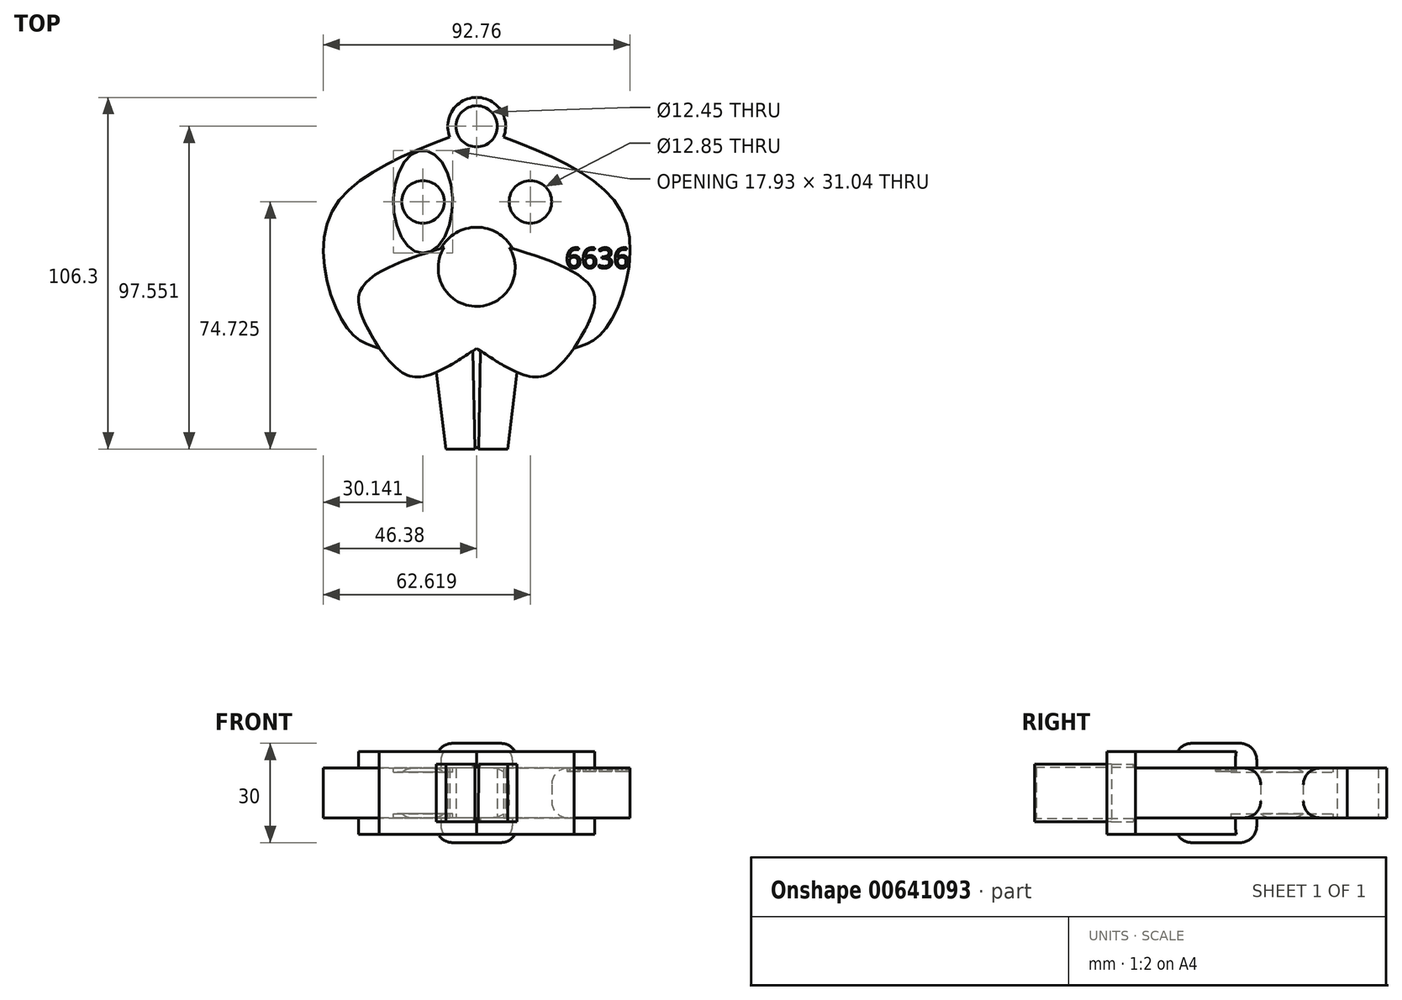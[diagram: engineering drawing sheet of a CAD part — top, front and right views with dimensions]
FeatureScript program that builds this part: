
annotation { "Feature Type Name" : "Feature", "Feature Type Description" : "" }
export const myFeature = defineFeature(function(context is Context, id is Id, definition is map)
    precondition{}
    {
        {
            var Q0;
            Q0=qCreatedBy(makeId("Top.planeOp"),FACE);
            var sketch = newSketch(context, id + "F0", { "sketchPlane" : qUnion([Q0])});
            skCircle(sketch, "E0", {"center": v(0, 42.8) * mm, "radius": 8.75 * mm});
            skFitSpline(sketch, "E1", {"points": [v(-8.15, 39.62) * mm, v(-44.98, 14.23) * mm, v(-38.66, -18.83) * mm, v(-29.46, -24.29) * mm], "startDerivative": vector(-114.3, -45.3) * mm, "endDerivative": vector(44.9, -12.6) * mm});
            skFitSpline(sketch, "E2", {"points": [v(-29.46, -24.29) * mm, v(-35.2, -7.04) * mm, v(-10.8, 5.9) * mm], "startDerivative": vector(-25.42, 41.75) * mm, "endDerivative": vector(58.9, 18.22) * mm});
            skCircle(sketch, "E3", {"center": v(0, 0) * mm, "radius": 12.3 * mm});
            skFitSpline(sketch, "E4", {"points": [v(-29.46, -24.29) * mm, v(-19.11, -32.9) * mm, v(0, -24.29) * mm], "startDerivative": vector(20.77, -27.15) * mm, "endDerivative": vector(37.53, 25.22) * mm});
            skLineSegment(sketch, "E5", {"start": v(-12.18, -31.55) * mm, "end": v(-9.34, -54.75) * mm});
            skLineSegment(sketch, "E6", {"start": v(-9.34, -54.75) * mm, "end": v(0, -54.75) * mm});
            skEllipse(sketch, "E7", {"center": v(-16.24, 19.97) * mm, "majorRadius": 15.52 * mm, "minorRadius": 8.97 * mm, "majorAxis": v(0, -1)});
            skFitSpline(sketch, "E8.MirrorCS", {"points": [v(8.15, 39.62) * mm, v(44.98, 14.23) * mm, v(38.66, -18.83) * mm, v(29.46, -24.29) * mm], "startDerivative": vector(114.3, -45.3) * mm, "endDerivative": vector(-44.9, -12.6) * mm});
            skEllipse(sketch, "E9.MirrorC", {"center": v(16.24, 19.97) * mm, "majorRadius": 15.52 * mm, "minorRadius": 8.97 * mm, "majorAxis": v(0, -1)});
            skFitSpline(sketch, "E10.MirrorCS", {"points": [v(29.46, -24.29) * mm, v(35.2, -7.04) * mm, v(10.8, 5.9) * mm], "startDerivative": vector(25.42, 41.75) * mm, "endDerivative": vector(-58.9, 18.22) * mm});
            skFitSpline(sketch, "E11.MirrorCS", {"points": [v(29.46, -24.29) * mm, v(19.11, -32.9) * mm, v(0, -24.29) * mm], "startDerivative": vector(-20.77, -27.15) * mm, "endDerivative": vector(-37.53, 25.22) * mm});
            skLineSegment(sketch, "E12.MirrorCS", {"start": v(12.18, -31.55) * mm, "end": v(9.34, -54.75) * mm});
            skLineSegment(sketch, "E13.MirrorCS", {"start": v(9.34, -54.75) * mm, "end": v(0, -54.75) * mm});
            skLineSegment(sketch, "E14", {"start": v(0, -54.75) * mm, "end": v(0, -24.29) * mm});
            skCircle(sketch, "E15", {"center": v(-16.24, 19.97) * mm, "radius": 6.43 * mm});
            skCircle(sketch, "E16.MirrorC", {"center": v(16.24, 19.97) * mm, "radius": 6.43 * mm});
            skCircle(sketch, "E17", {"center": v(0, 42.8) * mm, "radius": 6.22 * mm});
            skSolve(sketch);
        }
        {
            var Q0;
            {var subQ3=sQuery(id+"F0.wireOp",EDGE,"E1");Q0=makeQuery(id+"F0.imprint","IMPRINT",FACE,{"disambiguationData":[TD([[makeQuery(id+"F0.imprint","IMPRINT",EDGE,{"derivedFrom":subQ3}),1.0]])]});}
            extrude(context, id + "F1", {"entities" : qUnion([Q0]), "endBound" : BoundingType.SYMMETRIC, "depth" : 15 * mm, "offsetDistance" : 25 * mm});
        }
        {
            var Q0;
            {var subQ4=sQuery(id+"F0.wireOp",EDGE,"E2");Q0=makeQuery(id+"F0.imprint","IMPRINT",FACE,{"disambiguationData":[TD([[makeQuery(id+"F0.imprint","IMPRINT",EDGE,{"derivedFrom":subQ4}),-1.0]])]});}
            extrude(context, id + "F2", {"entities" : qUnion([Q0]), "operationType" : NewBodyOperationType.ADD, "endBound" : BoundingType.SYMMETRIC, "depth" : 25 * mm, "offsetDistance" : 25 * mm});
        }
        {
            var Q0;
            {var subQ2=sQuery(id+"F0.wireOp",EDGE,"E5");Q0=makeQuery(id+"F0.imprint","IMPRINT",FACE,{"disambiguationData":[TD([[makeQuery(id+"F0.imprint","IMPRINT",EDGE,{"derivedFrom":subQ2}),1.0]])]});}
            var Q1;
            {var subQ2=sQuery(id+"F0.wireOp",EDGE,"E12.MirrorCS");Q1=makeQuery(id+"F0.imprint","IMPRINT",FACE,{"disambiguationData":[TD([[makeQuery(id+"F0.imprint","IMPRINT",EDGE,{"derivedFrom":subQ2}),-1.0]])]});}
            extrude(context, id + "F3", {"entities" : qUnion([Q0, Q1]), "operationType" : NewBodyOperationType.ADD, "endBound" : BoundingType.SYMMETRIC, "depth" : 17.5 * mm, "offsetDistance" : 25 * mm});
        }
        {
            var Q0;
            {var subQ0=sQuery(id+"F0.wireOp",EDGE,"E3");var subQ1=makeQuery(id+"F0.imprint","INTERSECT",VERTEX,{"derivedFrom":[sQuery(id+"F0.wireOp",EDGE,"E2"),subQ0]});Q0=makeQuery(id+"F0.imprint","IMPRINT",FACE,{"disambiguationData":[TD([[makeQuery(id+"F0.imprint","IMPRINT",EDGE,{"disambiguationData":[TD([[subQ1,1.0]])],"derivedFrom":subQ0}),1.0]])]});}
            extrude(context, id + "F4", {"entities" : qUnion([Q0]), "operationType" : NewBodyOperationType.ADD, "endBound" : BoundingType.SYMMETRIC, "depth" : 30 * mm, "offsetDistance" : 25 * mm});
        }
        {
            var Q0;
            Q0=makeQuery(id+"F0.imprint","IMPRINT",FACE,{"disambiguationData":[TD([[makeQuery(id+"F0.imprint","IMPRINT",EDGE,{"derivedFrom":sQuery(id+"F0.wireOp",EDGE,"E7")}),1.0]])]});
            var Q1;
            Q1=makeQuery(id+"F0.imprint","IMPRINT",FACE,{"disambiguationData":[TD([[makeQuery(id+"F0.imprint","IMPRINT",EDGE,{"derivedFrom":sQuery(id+"F0.wireOp",EDGE,"E9.MirrorC")}),1.0]])]});
            extrude(context, id + "F5", {"entities" : qUnion([Q0, Q1]), "operationType" : NewBodyOperationType.ADD, "endBound" : BoundingType.SYMMETRIC, "depth" : 12.5 * mm, "offsetDistance" : 25 * mm});
        }
        {
            var Q0;
            {var subQ0=sQuery(id+"F0.wireOp",EDGE,"E0");var subQ1=makeQuery(id+"F0.imprint","INTERSECT",VERTEX,{"derivedFrom":[subQ0,sQuery(id+"F0.wireOp",EDGE,"E1")]});Q0=makeQuery(id+"F0.imprint","IMPRINT",FACE,{"disambiguationData":[TD([[makeQuery(id+"F0.imprint","IMPRINT",EDGE,{"disambiguationData":[TD([[subQ1,-1.0]])],"derivedFrom":subQ0}),1.0]])]});}
            extrude(context, id + "F6", {"entities" : qUnion([Q0]), "operationType" : NewBodyOperationType.ADD, "endBound" : BoundingType.SYMMETRIC, "depth" : 15 * mm, "offsetDistance" : 25 * mm});
        }
        {
            var Q0;
            Q0=makeQuery(id+"F0.imprint","IMPRINT",FACE,{"disambiguationData":[TD([[makeQuery(id+"F0.imprint","IMPRINT",EDGE,{"derivedFrom":sQuery(id+"F0.wireOp",EDGE,"E15")}),1.0]])]});
            var Q1;
            Q1=makeQuery(id+"F0.imprint","IMPRINT",FACE,{"disambiguationData":[TD([[makeQuery(id+"F0.imprint","IMPRINT",EDGE,{"derivedFrom":sQuery(id+"F0.wireOp",EDGE,"E16.MirrorC")}),-1.0]])]});
            extrude(context, id + "F7", {"entities" : qUnion([Q0, Q1]), "operationType" : NewBodyOperationType.ADD, "endBound" : BoundingType.SYMMETRIC, "depth" : 15 * mm, "offsetDistance" : 25 * mm});
        }
        {
            var Q0;
            Q0=makeQuery(id+"F3.opExtrude","CAP_FACE",FACE,{"disambiguationData":[OSD([sQuery(id+"F0.wireOp",EDGE,"E4"),sQuery(id+"F0.wireOp",EDGE,"E5"),sQuery(id+"F0.wireOp",EDGE,"E6"),sQuery(id+"F0.wireOp",EDGE,"E11.MirrorCS"),sQuery(id+"F0.wireOp",EDGE,"E12.MirrorCS"),sQuery(id+"F0.wireOp",EDGE,"E13.MirrorCS")])],"isStart":false});
            var sketch = newSketch(context, id + "F8", { "sketchPlane" : qUnion([Q0])});
            skLineSegment(sketch, "E18", {"start": v(-0.56, -54.75) * mm, "end": v(-1.1, -25.02) * mm});
            skLineSegment(sketch, "E19.MirrorCS", {"start": v(0.56, -54.75) * mm, "end": v(1.1, -25.02) * mm});
            skSolve(sketch);
        }
        {
            var Q0;
            Q0=makeQuery(id+"F3.opExtrude","CAP_FACE",FACE,{"disambiguationData":[OSD([sQuery(id+"F0.wireOp",EDGE,"E4"),sQuery(id+"F0.wireOp",EDGE,"E5"),sQuery(id+"F0.wireOp",EDGE,"E6"),sQuery(id+"F0.wireOp",EDGE,"E11.MirrorCS"),sQuery(id+"F0.wireOp",EDGE,"E12.MirrorCS"),sQuery(id+"F0.wireOp",EDGE,"E13.MirrorCS")])],"isStart":true});
            var sketch = newSketch(context, id + "F9", { "sketchPlane" : qUnion([Q0])});
            skLineSegment(sketch, "E20", {"start": v(0.54, 54.75) * mm, "end": v(1.09, 25.02) * mm});
            skLineSegment(sketch, "E21.MirrorCS", {"start": v(-0.54, 54.75) * mm, "end": v(-1.09, 25.02) * mm});
            skSolve(sketch);
        }
        {
            var Q0;
            {var subQ4=sQuery(id+"F9.wireOp",EDGE,"E20");Q0=makeQuery(id+"F9.imprint","IMPRINT",FACE,{"disambiguationData":[TD([[makeQuery(id+"F9.imprint","IMPRINT",EDGE,{"derivedFrom":subQ4}),-1.0]])]});}
            extrude(context, id + "F10", {"entities" : qUnion([Q0]), "operationType" : NewBodyOperationType.REMOVE, "oppositeDirection" : true, "depth" : 1 * mm, "offsetDistance" : 25 * mm});
        }
        {
            var Q0;
            {var subQ3=sQuery(id+"F8.wireOp",EDGE,"E18");Q0=makeQuery(id+"F8.imprint","IMPRINT",FACE,{"disambiguationData":[TD([[makeQuery(id+"F8.imprint","IMPRINT",EDGE,{"derivedFrom":subQ3}),-1.0]])]});}
            extrude(context, id + "F11", {"entities" : qUnion([Q0]), "operationType" : NewBodyOperationType.REMOVE, "oppositeDirection" : true, "depth" : 1 * mm, "offsetDistance" : 25 * mm});
        }
        {
            var Q0;
            Q0=makeQuery(id+"F3.opExtrude","SWEPT_FACE",FACE,{"disambiguationData":[OSD([sQuery(id+"F0.wireOp",EDGE,"E6"),sQuery(id+"F0.wireOp",EDGE,"E13.MirrorCS")])]});
            var sketch = newSketch(context, id + "F12", { "sketchPlane" : qUnion([Q0])});
            skLineSegment(sketch, "E22", {"start": v(-0.56, 7.75) * mm, "end": v(-0.54, -7.75) * mm});
            skLineSegment(sketch, "E23", {"start": v(0.54, -7.75) * mm, "end": v(0.56, 7.75) * mm});
            skSolve(sketch);
        }
        {
            var Q0;
            Q0=makeQuery(id+"F12.imprint","IMPRINT",FACE,{"disambiguationData":[TD([[makeQuery(id+"F12.imprint","IMPRINT",EDGE,{"derivedFrom":sQuery(id+"F12.wireOp",EDGE,"E22")}),1.0]])]});
            extrude(context, id + "F13", {"entities" : qUnion([Q0]), "operationType" : NewBodyOperationType.REMOVE, "endBound" : BoundingType.SYMMETRIC, "depth" : 1 * mm, "offsetDistance" : 25 * mm});
        }
        {
            var Q0;
            Q0=makeQuery(id+"F4.opExtrude","CAP_EDGE",EDGE,{"disambiguationData":[OSD([sQuery(id+"F0.wireOp",EDGE,"E3")])],"isStart":true});
            var Q1;
            Q1=makeQuery(id+"F4.opExtrude","CAP_EDGE",EDGE,{"disambiguationData":[OSD([sQuery(id+"F0.wireOp",EDGE,"E3")])],"isStart":false});
            var Q2;
            Q2=makeQuery(id+"F7.opExtrude","CAP_EDGE",EDGE,{"disambiguationData":[OSD([sQuery(id+"F0.wireOp",EDGE,"E16.MirrorC")])],"isStart":true});
            var Q3;
            Q3=makeQuery(id+"F7.opExtrude","CAP_EDGE",EDGE,{"disambiguationData":[OSD([sQuery(id+"F0.wireOp",EDGE,"E15")])],"isStart":true});
            var Q4;
            Q4=makeQuery(id+"F7.opExtrude","CAP_EDGE",EDGE,{"disambiguationData":[OSD([sQuery(id+"F0.wireOp",EDGE,"E16.MirrorC")])],"isStart":false});
            var Q5;
            Q5=makeQuery(id+"F7.opExtrude","CAP_EDGE",EDGE,{"disambiguationData":[OSD([sQuery(id+"F0.wireOp",EDGE,"E15")])],"isStart":false});
            fillet(context, id + "F14", {"entities" : qUnion([Q0, Q1, Q2, Q3, Q4, Q5]), "radius" : 5 * mm, "tangentPropagation" : true, "allowEdgeOverflow" : false});
        }
        {
            var Q0;
            {var subQ0=sQuery(id+"F0.wireOp",EDGE,"E0");Q0=makeQuery(id+"F6.boolean.opBoolean","MERGE",FACE,{"derivedFrom":[makeQuery(id+"F1.opExtrude","CAP_FACE",FACE,{"disambiguationData":[OSD([subQ0,sQuery(id+"F0.wireOp",EDGE,"E1"),sQuery(id+"F0.wireOp",EDGE,"E2"),sQuery(id+"F0.wireOp",EDGE,"E3"),sQuery(id+"F0.wireOp",EDGE,"E7"),sQuery(id+"F0.wireOp",EDGE,"E8.MirrorCS"),sQuery(id+"F0.wireOp",EDGE,"E9.MirrorC"),sQuery(id+"F0.wireOp",EDGE,"E10.MirrorCS")])],"isStart":false}),makeQuery(id+"F6.opExtrude","CAP_FACE",FACE,{"disambiguationData":[OSD([subQ0,sQuery(id+"F0.wireOp",EDGE,"E17")])],"isStart":false})]});}
            var sketch = newSketch(context, id + "F15", { "sketchPlane" : qUnion([Q0])});
            skText(sketch, "E24", { "text": "6636", "fontName": "OpenSans-Regular.ttf"});
            const initialGuessF15  = {"E24": [0.02683, 0, 1, 0, 0.0061]};
            skSetInitialGuess(sketch, initialGuessF15);
            skSolve(sketch);
        }
        {
            var Q0;
            Q0 = qSketchRegion(id + "F15", true);
            var Q1;
            Q1 = qConstructionFilter(qBodyType(qCreatedBy(id + "F15" ,EDGE), BodyType.WIRE), ConstructionObject.NO);
            extrude(context, id + "F16", {"entities" : qUnion([Q0]), "operationType" : NewBodyOperationType.REMOVE, "surfaceEntities" : qUnion([Q1]), "endBound" : BoundingType.SYMMETRIC, "depth" : 2 * mm, "offsetDistance" : 25 * mm});
        }
    });
